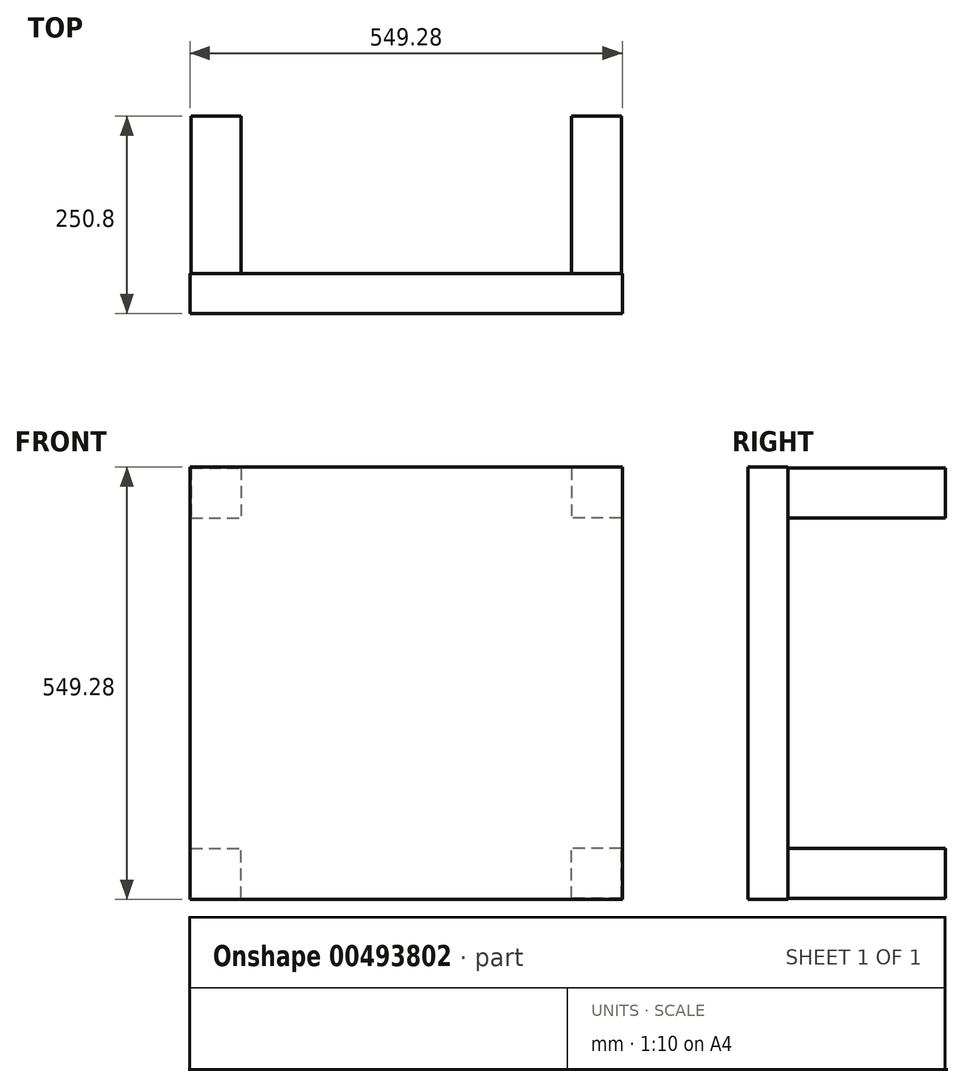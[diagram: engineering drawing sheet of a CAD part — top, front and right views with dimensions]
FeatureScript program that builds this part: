
annotation { "Feature Type Name" : "Feature", "Feature Type Description" : "" }
export const myFeature = defineFeature(function(context is Context, id is Id, definition is map)
    precondition{}
    {
        {
            var Q0;
            Q0=qCreatedBy(makeId("Front.planeOp"),FACE);
            var sketch = newSketch(context, id + "F0", { "sketchPlane" : qUnion([Q0])});
            skLineSegment(sketch, "E0.bottom", {"start": v(274.64, 274.64) * mm, "end": v(-274.64, 274.64) * mm});
            skLineSegment(sketch, "E0.top", {"start": v(274.64, -274.64) * mm, "end": v(-274.64, -274.64) * mm});
            skLineSegment(sketch, "E0.left", {"start": v(274.64, 274.64) * mm, "end": v(274.64, -274.64) * mm});
            skLineSegment(sketch, "E0.right", {"start": v(-274.64, 274.64) * mm, "end": v(-274.64, -274.64) * mm});
            skPoint(sketch, "E0.middle", {"position": v(0, 0) * mm});
            skLineSegment(sketch, "E1", {"start": v(-274.64, 274.64) * mm, "end": v(-273.37, 274.64) * mm, "construction": true});
            skLineSegment(sketch, "E2", {"start": v(-273.37, 274.64) * mm, "end": v(-273.37, 273.37) * mm, "construction": true});
            skPoint(sketch, "E3", {"position": v(-273.37, 273.37) * mm});
            skLineSegment(sketch, "E4.bottom", {"start": v(-273.37, 273.37) * mm, "end": v(-209.87, 273.37) * mm});
            skLineSegment(sketch, "E4.top", {"start": v(-273.37, 209.87) * mm, "end": v(-209.87, 209.87) * mm});
            skLineSegment(sketch, "E4.left", {"start": v(-273.37, 273.37) * mm, "end": v(-273.37, 209.87) * mm});
            skLineSegment(sketch, "E4.right", {"start": v(-209.87, 273.37) * mm, "end": v(-209.87, 209.87) * mm});
            skLineSegment(sketch, "E5", {"start": v(0, 0) * mm, "end": v(0, 20.48) * mm});
            skLineSegment(sketch, "E6", {"start": v(0, 20.48) * mm, "end": v(0, 0) * mm});
            skLineSegment(sketch, "E7", {"start": v(28.9, 0) * mm, "end": v(0, 0) * mm});
            skLineSegment(sketch, "E8.MirrorCS", {"start": v(209.87, 273.37) * mm, "end": v(209.87, 209.87) * mm});
            skLineSegment(sketch, "E9.MirrorCS", {"start": v(273.37, 209.87) * mm, "end": v(209.87, 209.87) * mm});
            skLineSegment(sketch, "E10.MirrorCS", {"start": v(273.37, 273.37) * mm, "end": v(273.37, 209.87) * mm});
            skLineSegment(sketch, "E11.MirrorCS", {"start": v(273.37, 273.37) * mm, "end": v(209.87, 273.37) * mm});
            skLineSegment(sketch, "E12.MirrorCS", {"start": v(-209.87, -273.37) * mm, "end": v(-209.87, -209.87) * mm});
            skLineSegment(sketch, "E13.MirrorCS", {"start": v(-273.37, -209.87) * mm, "end": v(-209.87, -209.87) * mm});
            skLineSegment(sketch, "E14.MirrorCS", {"start": v(-273.37, -273.37) * mm, "end": v(-273.37, -209.87) * mm});
            skLineSegment(sketch, "E15.MirrorCS", {"start": v(-273.37, -273.37) * mm, "end": v(-209.87, -273.37) * mm});
            skLineSegment(sketch, "E16.MirrorCS", {"start": v(273.37, -209.87) * mm, "end": v(209.87, -209.87) * mm});
            skLineSegment(sketch, "E17.MirrorCS", {"start": v(209.87, -273.37) * mm, "end": v(209.87, -209.87) * mm});
            skLineSegment(sketch, "E18.MirrorCS", {"start": v(273.37, -273.37) * mm, "end": v(273.37, -209.87) * mm});
            skLineSegment(sketch, "E19.MirrorCS", {"start": v(273.37, -273.37) * mm, "end": v(209.87, -273.37) * mm});
            skSolve(sketch);
        }
        {
            var Q0;
            Q0=makeQuery(id+"F0.imprint","IMPRINT",FACE,{"disambiguationData":[TD([[makeQuery(id+"F0.imprint","IMPRINT",EDGE,{"derivedFrom":sQuery(id+"F0.wireOp",EDGE,"E0.bottom")}),1.0]])]});
            var Q1;
            Q1=makeQuery(id+"F0.imprint","IMPRINT",FACE,{"disambiguationData":[TD([[makeQuery(id+"F0.imprint","IMPRINT",EDGE,{"derivedFrom":sQuery(id+"F0.wireOp",EDGE,"E8.MirrorCS")}),1.0]])]});
            var Q2;
            Q2=makeQuery(id+"F0.imprint","IMPRINT",FACE,{"disambiguationData":[TD([[makeQuery(id+"F0.imprint","IMPRINT",EDGE,{"derivedFrom":sQuery(id+"F0.wireOp",EDGE,"E4.bottom")}),-1.0]])]});
            var Q3;
            Q3=makeQuery(id+"F0.imprint","IMPRINT",FACE,{"disambiguationData":[TD([[makeQuery(id+"F0.imprint","IMPRINT",EDGE,{"derivedFrom":sQuery(id+"F0.wireOp",EDGE,"E12.MirrorCS")}),1.0]])]});
            var Q4;
            Q4=makeQuery(id+"F0.imprint","IMPRINT",FACE,{"disambiguationData":[TD([[makeQuery(id+"F0.imprint","IMPRINT",EDGE,{"derivedFrom":sQuery(id+"F0.wireOp",EDGE,"E16.MirrorCS")}),1.0]])]});
            extrude(context, id + "F1", {"entities" : qUnion([Q0, Q1, Q2, Q3, Q4]), "depth" : 50.8 * mm});
        }
        {
            var Q0;
            Q0=makeQuery(id+"F0.imprint","IMPRINT",FACE,{"disambiguationData":[TD([[makeQuery(id+"F0.imprint","IMPRINT",EDGE,{"derivedFrom":sQuery(id+"F0.wireOp",EDGE,"E4.bottom")}),-1.0]])]});
            var Q1;
            Q1=makeQuery(id+"F0.imprint","IMPRINT",FACE,{"disambiguationData":[TD([[makeQuery(id+"F0.imprint","IMPRINT",EDGE,{"derivedFrom":sQuery(id+"F0.wireOp",EDGE,"E8.MirrorCS")}),1.0]])]});
            var Q2;
            Q2=makeQuery(id+"F0.imprint","IMPRINT",FACE,{"disambiguationData":[TD([[makeQuery(id+"F0.imprint","IMPRINT",EDGE,{"derivedFrom":sQuery(id+"F0.wireOp",EDGE,"E16.MirrorCS")}),1.0]])]});
            var Q3;
            Q3=makeQuery(id+"F0.imprint","IMPRINT",FACE,{"disambiguationData":[TD([[makeQuery(id+"F0.imprint","IMPRINT",EDGE,{"derivedFrom":sQuery(id+"F0.wireOp",EDGE,"E12.MirrorCS")}),1.0]])]});
            extrude(context, id + "F2", {"entities" : qUnion([Q0, Q1, Q2, Q3]), "operationType" : NewBodyOperationType.ADD, "oppositeDirection" : true, "depth" : 200 * mm, "offsetDistance" : 25 * mm});
        }
    });
